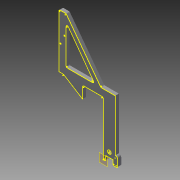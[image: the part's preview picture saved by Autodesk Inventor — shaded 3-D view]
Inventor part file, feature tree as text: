
AUTODESK INVENTOR PART (.ipt)
format: ipt  version: 2013 (Build 170138000, 138)  size: 207,872 bytes
history: native  units: in
note: dims shown in document units (in); Inventor stores cm internally (conversion verified against a paired STEP export)
features: fillet x6, sketch x3, extrude x3, plane x1
ambient origin geometry x8: Origin, YZ Plane, XZ Plane, XY Plane, X Axis, Y Axis, Z Axis, Center Point
feature tree (13):
  plane  "Work Plane1"
  sketch  "Sketch2"  dims[d0=0.25in d1=0.5in]
  extrude  "Extrusion4"  Depth=0.5in
  extrude  "Extrusion5"  Depth=0.25in
  fillet  "Fillet2"  Radius=6.375in
  fillet  "Fillet3"  Radius=0.3765in
  fillet  "Fillet4"  Radius=0.5in
  fillet  "Fillet5"  Radius=0.375in
  extrude  "Extrusion7"  Depth=0.75in
  fillet  "Fillet6"  Radius=2.15in
  fillet  "Fillet7"  Radius=1.25in
  sketch  "Sketch5"  dims[d8=5.875in d9=0.75in d12=2.15in d13=1.25in d14=2.0in d15=0.75in d19=3.0in d24=0.125in d25=0.573in d26=2.6125in d27=0.125in d29=3.5185in d32=0.175in d33=0.75in d34=4.8333in d36=3.0in d37=0.75in d38=0.75in d39=3.0in d40=3.0in d41=0.75in d42=0.375in d43=0.0in d44=0.375in d45=0.0in d50=0.0034in d51=0.5in d52=0.125in d53=0.125in d54=0.125in d55=0.125in d56=0.5in d57=0.375in d58=0.0in d59=0.125in d60=0.25in d61=0.5in]
  sketch  "Sketch4"  dims[d2=0.75in d3=0.25in d4=6.375in d5=0.3765in d6=0.5in d7=0.375in]
